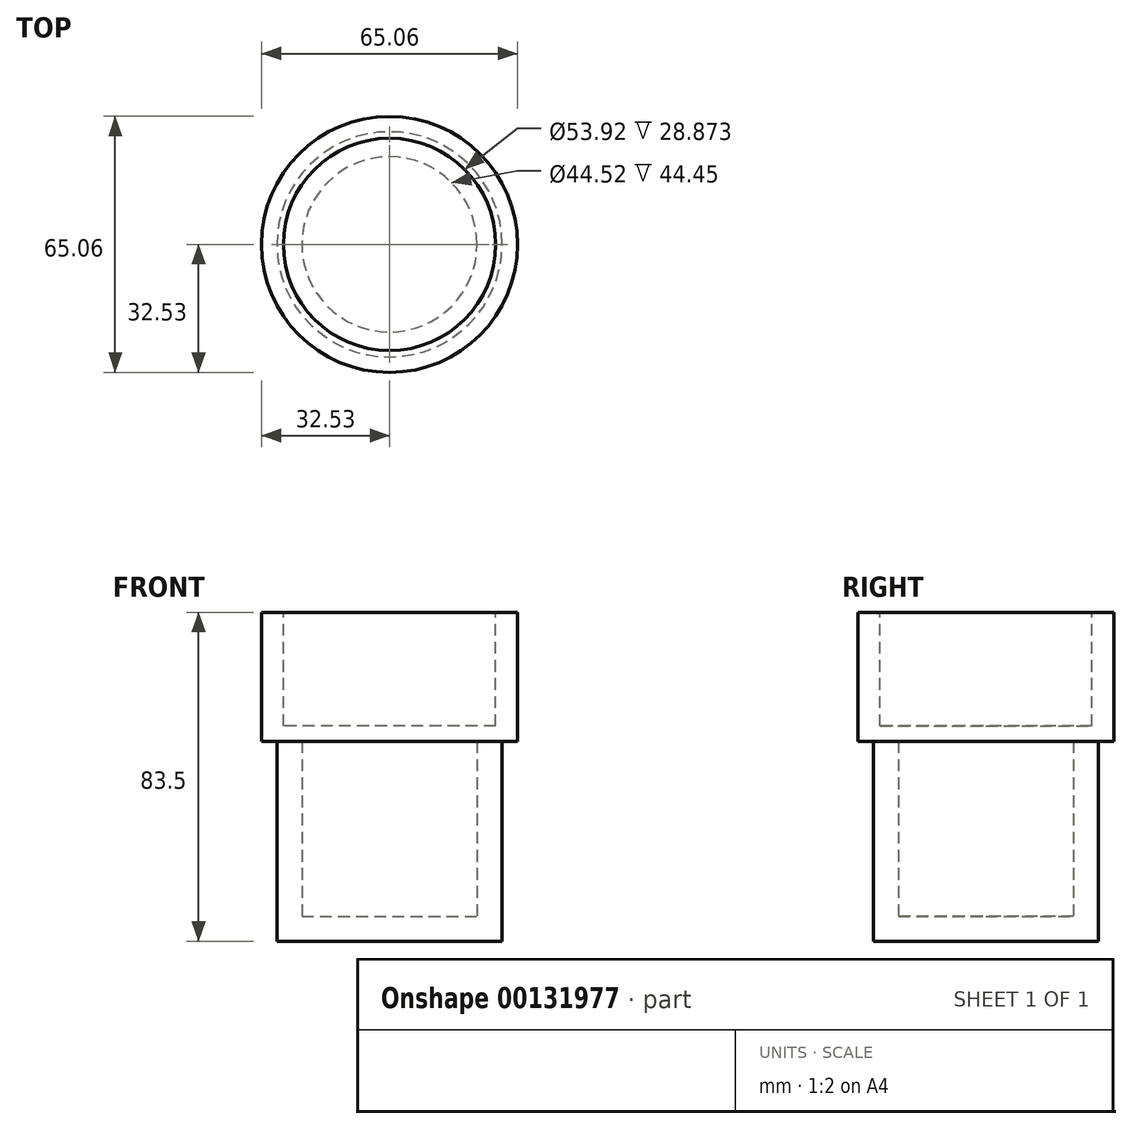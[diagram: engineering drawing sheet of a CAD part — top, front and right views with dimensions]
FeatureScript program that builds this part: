
annotation { "Feature Type Name" : "Feature", "Feature Type Description" : "" }
export const myFeature = defineFeature(function(context is Context, id is Id, definition is map)
    precondition{}
    {
        {
            var Q0;
            Q0=qCreatedBy(makeId("Front.planeOp"),FACE);
            var sketch = newSketch(context, id + "F0", { "sketchPlane" : qUnion([Q0])});
            skLineSegment(sketch, "E0", {"start": v(0, 0) * mm, "end": v(-32.53, 0) * mm});
            skLineSegment(sketch, "E1", {"start": v(-32.53, 0) * mm, "end": v(-32.53, 32.7) * mm});
            skLineSegment(sketch, "E2", {"start": v(-32.53, 32.7) * mm, "end": v(-26.96, 32.7) * mm});
            skLineSegment(sketch, "E3", {"start": v(-26.96, 32.7) * mm, "end": v(-26.96, 3.83) * mm});
            skLineSegment(sketch, "E4", {"start": v(-26.96, 3.83) * mm, "end": v(0, 3.83) * mm});
            skLineSegment(sketch, "E5", {"start": v(0, 3.83) * mm, "end": v(0, 0) * mm});
            skSolve(sketch);
        }
        {
            var Q0;
            Q0=makeQuery(id+"F0.imprint","IMPRINT",FACE,{"disambiguationData":[TD([[makeQuery(id+"F0.imprint","IMPRINT",EDGE,{"derivedFrom":sQuery(id+"F0.wireOp",EDGE,"E0")}),-1.0]])]});
            var Q1;
            Q1=sQuery(id+"F0.wireOp",EDGE,"E5");
            revolve(context, id + "F1", {"entities" : qUnion([Q0]), "axis" : qUnion([Q1]), "revolveType" : RevolveType.FULL});
        }
        {
            var Q0;
            Q0=qCreatedBy(makeId("Front.planeOp"),FACE);
            var sketch = newSketch(context, id + "F2", { "sketchPlane" : qUnion([Q0])});
            skLineSegment(sketch, "E6", {"start": v(-28.6, 0) * mm, "end": v(-28.6, -50.8) * mm});
            skLineSegment(sketch, "E7", {"start": v(-28.6, -50.8) * mm, "end": v(0, -50.8) * mm});
            skLineSegment(sketch, "E8", {"start": v(0, -50.8) * mm, "end": v(0, -44.45) * mm});
            skLineSegment(sketch, "E9", {"start": v(0, -44.45) * mm, "end": v(-22.26, -44.45) * mm});
            skLineSegment(sketch, "E10", {"start": v(-22.26, -44.45) * mm, "end": v(-22.26, 0) * mm});
            skLineSegment(sketch, "E11", {"start": v(-22.26, 0) * mm, "end": v(-28.6, 0) * mm});
            skSolve(sketch);
        }
        {
            var Q0;
            Q0=makeQuery(id+"F2.imprint","IMPRINT",FACE,{"disambiguationData":[TD([[makeQuery(id+"F2.imprint","IMPRINT",EDGE,{"derivedFrom":sQuery(id+"F2.wireOp",EDGE,"E6")}),1.0]])]});
            var Q1;
            Q1=sQuery(id+"F2.wireOp",EDGE,"E8");
            revolve(context, id + "F3", {"operationType" : NewBodyOperationType.ADD, "entities" : qUnion([Q0]), "axis" : qUnion([Q1]), "revolveType" : RevolveType.FULL});
        }
    });
